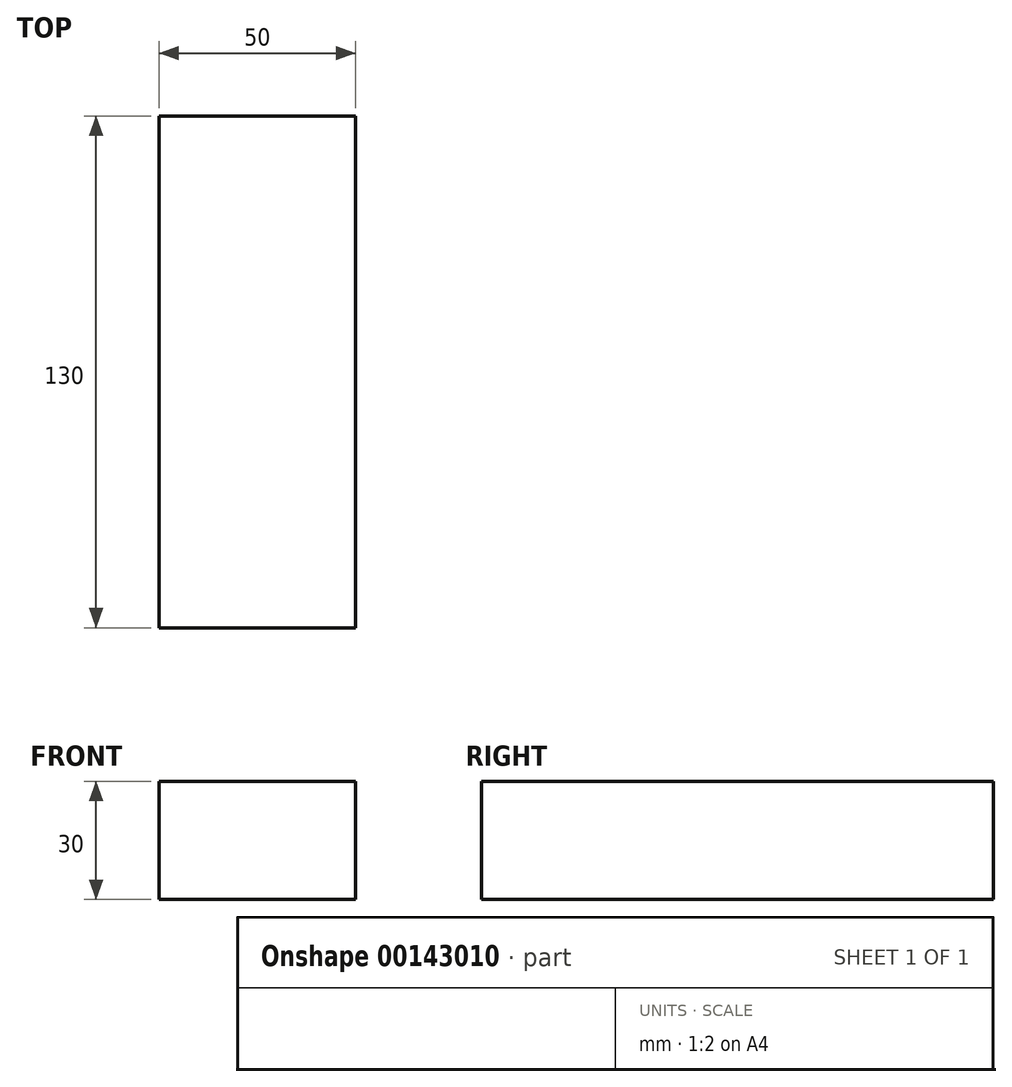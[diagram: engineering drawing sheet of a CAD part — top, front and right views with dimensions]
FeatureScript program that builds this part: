
annotation { "Feature Type Name" : "Feature", "Feature Type Description" : "" }
export const myFeature = defineFeature(function(context is Context, id is Id, definition is map)
    precondition{}
    {
        {
            var Q0;
            Q0=qCreatedBy(makeId("Top.planeOp"),FACE);
            var sketch = newSketch(context, id + "F0", { "sketchPlane" : qUnion([Q0])});
            skLineSegment(sketch, "E0.bottom", {"start": v(0, 0) * mm, "end": v(50, 0) * mm});
            skLineSegment(sketch, "E0.top", {"start": v(0, 130) * mm, "end": v(50, 130) * mm});
            skLineSegment(sketch, "E0.left", {"start": v(0, 0) * mm, "end": v(0, 130) * mm});
            skLineSegment(sketch, "E0.right", {"start": v(50, 0) * mm, "end": v(50, 130) * mm});
            skSolve(sketch);
        }
        {
            var Q0;
            Q0 = qSketchRegion(id + "F0", true);
            extrude(context, id + "F1", {"entities" : qUnion([Q0]), "depth" : 30 * mm});
        }
    });
